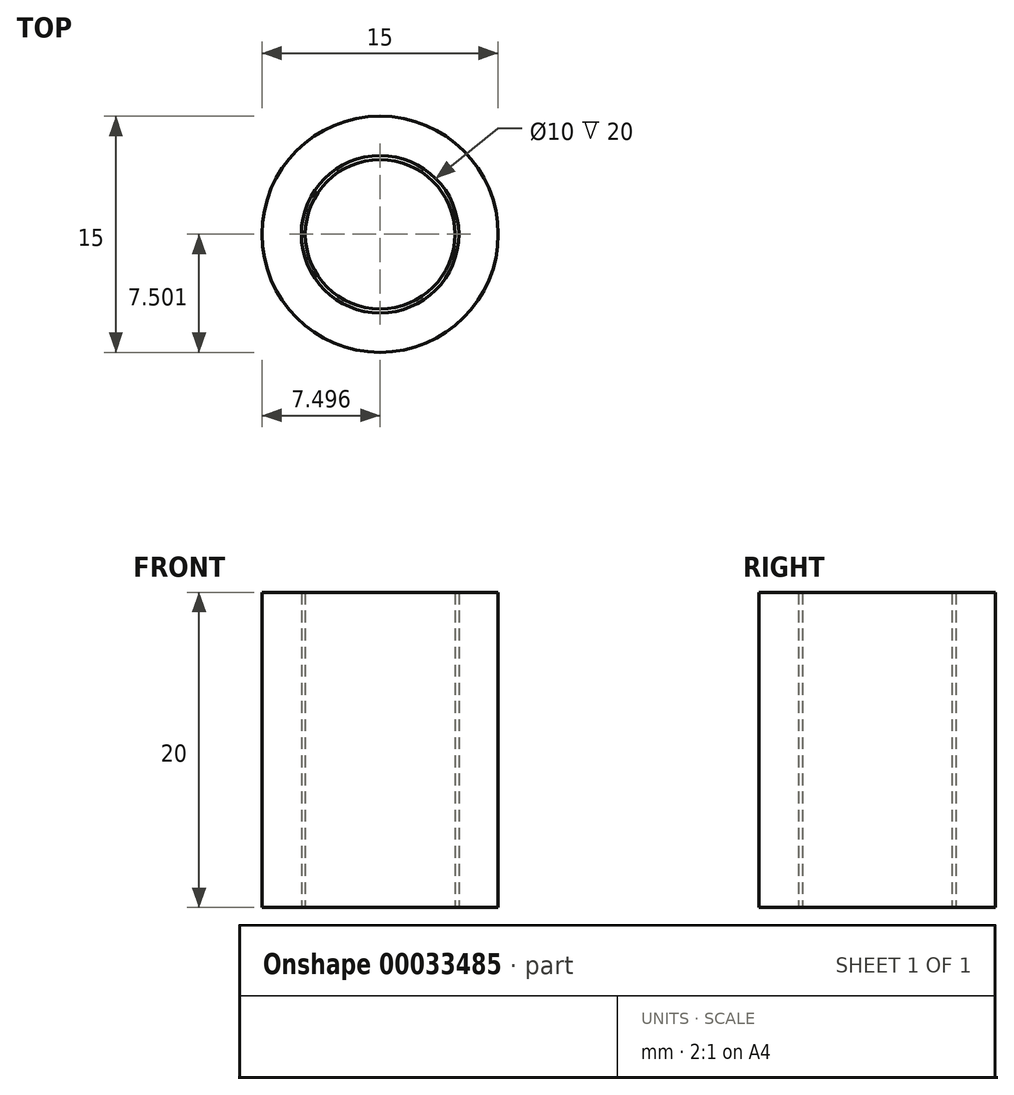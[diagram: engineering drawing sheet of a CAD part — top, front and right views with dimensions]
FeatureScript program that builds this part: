
annotation { "Feature Type Name" : "Feature", "Feature Type Description" : "" }
export const myFeature = defineFeature(function(context is Context, id is Id, definition is map)
    precondition{}
    {
        {
            var Q0;
            Q0=qCreatedBy(makeId("Top.planeOp"),FACE);
            var sketch = newSketch(context, id + "F0", { "sketchPlane" : qUnion([Q0])});
            skLineSegment(sketch, "E0.bottom", {"start": v(-75.04, 75.46) * mm, "end": v(74.96, 75.46) * mm});
            skLineSegment(sketch, "E0.top", {"start": v(-75.04, -74.54) * mm, "end": v(74.96, -74.54) * mm});
            skLineSegment(sketch, "E0.left", {"start": v(-75.04, 75.46) * mm, "end": v(-75.04, -74.54) * mm});
            skLineSegment(sketch, "E0.right", {"start": v(74.96, 75.46) * mm, "end": v(74.96, -74.54) * mm});
            skCircle(sketch, "E1", {"center": v(54.96, 55.46) * mm, "radius": 7.5 * mm});
            skCircle(sketch, "E2", {"center": v(54.96, 55.46) * mm, "radius": 5 * mm});
            skSolve(sketch);
        }
        {
            var Q0;
            Q0=makeQuery(id+"F0.imprint","IMPRINT",FACE,{"disambiguationData":[TD([[makeQuery(id+"F0.imprint","IMPRINT",EDGE,{"derivedFrom":sQuery(id+"F0.wireOp",EDGE,"E1")}),1.0]])]});
            var Q1;
            Q1 = qSketchRegion(id + "F2", true);
            extrude(context, id + "F1", {"entities" : qUnion([Q0, Q1]), "depth" : 20 * mm});
        }
        {
            var Q0;
            Q0=qCreatedBy(makeId("Top.planeOp"),FACE);
            var sketch = newSketch(context, id + "F2", { "sketchPlane" : qUnion([Q0])});
            skPoint(sketch, "E3", {"position": v(54.96, 55.46) * mm});
            skCircle(sketch, "E4", {"center": v(54.96, 55.46) * mm, "radius": 4.75 * mm});
            skSolve(sketch);
        }
        {
            var Q0;
            Q0=makeQuery(id+"F2.imprint","IMPRINT",FACE,{"disambiguationData":[TD([[makeQuery(id+"F2.imprint","IMPRINT",EDGE,{"derivedFrom":sQuery(id+"F2.wireOp",EDGE,"E4")}),1.0]])]});
            extrude(context, id + "F3", {"entities" : qUnion([Q0]), "depth" : 20 * mm});
        }
    });
